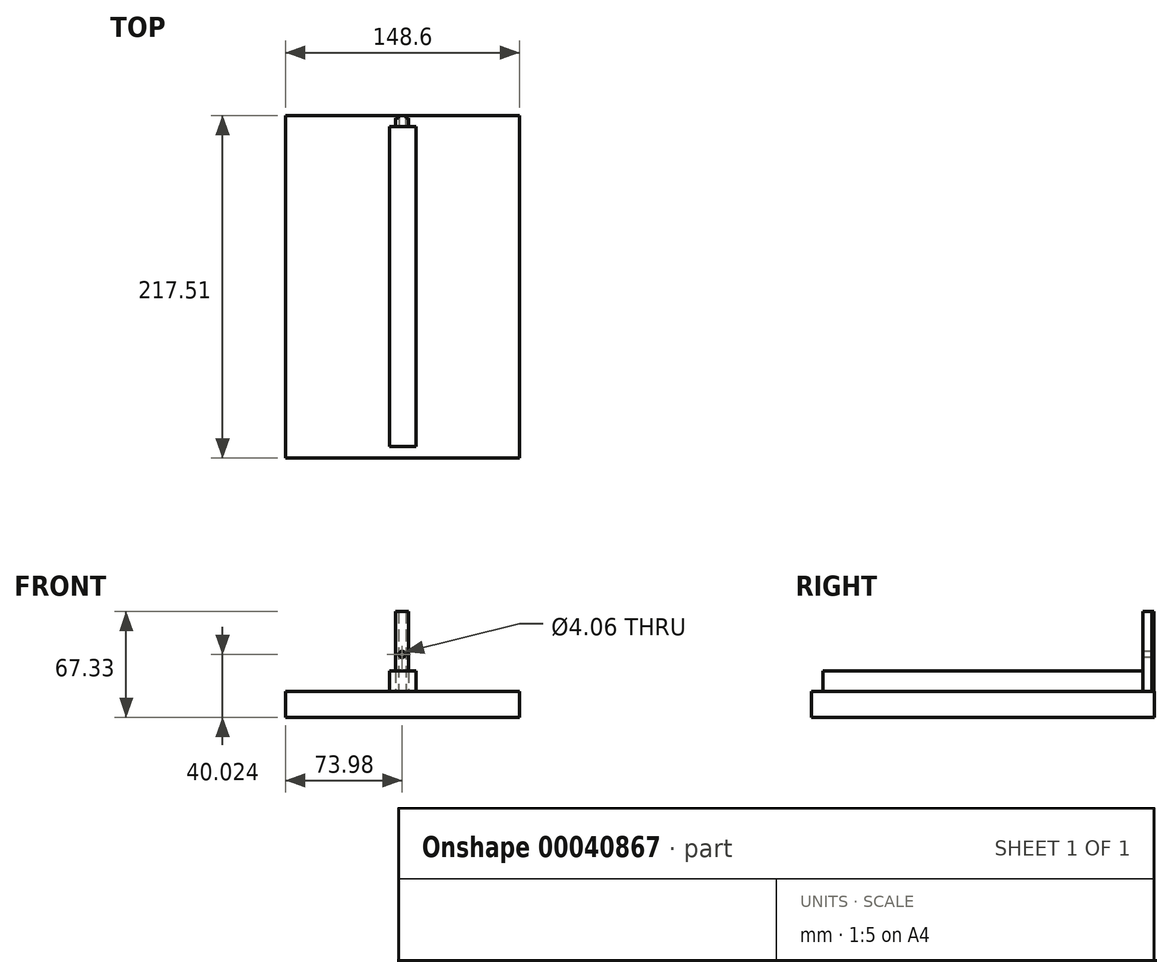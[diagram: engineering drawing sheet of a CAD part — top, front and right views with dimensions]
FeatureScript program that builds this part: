
annotation { "Feature Type Name" : "Feature", "Feature Type Description" : "" }
export const myFeature = defineFeature(function(context is Context, id is Id, definition is map)
    precondition{}
    {
        {
            var Q0;
            Q0=qCreatedBy(makeId("Top.planeOp"),FACE);
            var sketch = newSketch(context, id + "F0", { "sketchPlane" : qUnion([Q0])});
            skLineSegment(sketch, "E0.rect.bottom", {"start": v(4.76, -2.8) * mm, "end": v(-4.76, -2.8) * mm});
            skLineSegment(sketch, "E0.rect.top", {"start": v(4.76, 2.8) * mm, "end": v(2.98, 2.8) * mm});
            skPoint(sketch, "E0.rect.middle", {"position": v(0, 0) * mm});
            skPoint(sketch, "E1", {"position": v(2.98, 2.8) * mm});
            skPoint(sketch, "E2.MirrorP", {"position": v(-3.2, 2.8) * mm});
            skLineSegment(sketch, "E3.MirrorCS", {"start": v(0.01, 2.8) * mm, "end": v(0.01, 4.2) * mm});
            skLineSegment(sketch, "E4", {"start": v(0.01, 4.2) * mm, "end": v(2.98, 4.2) * mm});
            skPoint(sketch, "E5.orphan", {"position": v(0, 4.1) * mm});
            skLineSegment(sketch, "E6.trimOffspring", {"start": v(0.01, 2.8) * mm, "end": v(-4.76, 2.8) * mm});
            skLineSegment(sketch, "E7", {"start": v(0, 4.1) * mm, "end": v(0, 5.18) * mm});
            skLineSegment(sketch, "E8.MirrorCS", {"start": v(-0.01, 4.2) * mm, "end": v(-2.98, 4.2) * mm});
            skLineSegment(sketch, "E9.MirrorCS", {"start": v(-0.01, 2.8) * mm, "end": v(-0.01, 4.2) * mm});
            skLineSegment(sketch, "E10", {"start": v(-0.01, 4.2) * mm, "end": v(0.01, 4.2) * mm});
            skLineSegment(sketch, "E11", {"start": v(-2.36, 4.2) * mm, "end": v(-2.36, 2.8) * mm});
            skLineSegment(sketch, "E12", {"start": v(2.98, 2.8) * mm, "end": v(-0.01, 2.8) * mm});
            skLineSegment(sketch, "E13", {"start": v(2.36, 4.2) * mm, "end": v(2.36, 2.8) * mm});
            skLineSegment(sketch, "E14", {"start": v(-4.13, 2.8) * mm, "end": v(-4.13, -2.8) * mm});
            skLineSegment(sketch, "E15", {"start": v(4.13, 2.8) * mm, "end": v(4.13, -2.8) * mm});
            skSolve(sketch);
        }
        {
            var Q0;
            Q0 = qSketchRegion(id + "F0", true);
            extrude(context, id + "F1", {"entities" : qUnion([Q0]), "depth" : 50.8 * mm});
        }
        {
            var Q0;
            Q0=makeQuery(id+"F1.opExtrude","SWEPT_FACE",FACE,{"disambiguationData":[OSD([sQuery(id+"F0.wireOp",EDGE,"E0.rect.bottom")])]});
            var sketch = newSketch(context, id + "F2", { "sketchPlane" : qUnion([Q0])});
            skCircle(sketch, "E16", {"center": v(0, 23.5) * mm, "radius": 2.03 * mm});
            skSolve(sketch);
        }
        {
            var Q0;
            Q0=sQuery(id+"F2.wireOp",VERTEX,"E16.center");
            var Q1;
            Q1=makeQuery(id+"F1.opExtrude","SWEPT_BODY",BODY,{"disambiguationData":[OSD([sQuery(id+"F0.wireOp",EDGE,"E0.rect.bottom"),sQuery(id+"F0.wireOp",EDGE,"E0.rect.top"),sQuery(id+"F0.wireOp",EDGE,"E4"),sQuery(id+"F0.wireOp",EDGE,"E6.trimOffspring"),sQuery(id+"F0.wireOp",EDGE,"E8.MirrorCS"),sQuery(id+"F0.wireOp",EDGE,"E10"),sQuery(id+"F0.wireOp",EDGE,"E11"),sQuery(id+"F0.wireOp",EDGE,"E12"),sQuery(id+"F0.wireOp",EDGE,"E13"),sQuery(id+"F0.wireOp",EDGE,"E14"),sQuery(id+"F0.wireOp",EDGE,"E15")])]});
            hole(context, id + "F3", {"style" : HoleStyle.SIMPLE, "holeDiameter" : 4.06 * mm, "endStyle" : HoleEndStyle.THROUGH, "locations" : qUnion([Q0]), "scope" : qUnion([Q1])});
        }
        {
            var Q0;
            Q0=makeQuery(id+"F1.opExtrude","SWEPT_FACE",FACE,{"disambiguationData":[OSD([sQuery(id+"F0.wireOp",EDGE,"E0.rect.bottom")])]});
            var sketch = newSketch(context, id + "F4", { "sketchPlane" : qUnion([Q0])});
            skLineSegment(sketch, "E17.rect.bottom", {"start": v(8.76, -0.02) * mm, "end": v(-8.12, -0.02) * mm});
            skLineSegment(sketch, "E17.rect.top", {"start": v(8.76, 12.93) * mm, "end": v(-8.12, 12.93) * mm});
            skLineSegment(sketch, "E17.rect.left", {"start": v(8.76, -0.02) * mm, "end": v(8.76, 12.93) * mm});
            skLineSegment(sketch, "E17.rect.right", {"start": v(-8.12, -0.02) * mm, "end": v(-8.12, 12.93) * mm});
            skPoint(sketch, "E17.rect.middle", {"position": v(0.32, 6.45) * mm});
            skSolve(sketch);
        }
        {
            var Q0;
            Q0 = qSketchRegion(id + "F4", true);
            extrude(context, id + "F5", {"entities" : qUnion([Q0]), "operationType" : NewBodyOperationType.ADD, "depth" : 203.2 * mm});
        }
        {
            var Q0;
            Q0=makeQuery(id+"F5.opExtrude","SWEPT_FACE",FACE,{"disambiguationData":[OSD([sQuery(id+"F4.wireOp",EDGE,"E17.rect.bottom")])]});
            var sketch = newSketch(context, id + "F6", { "sketchPlane" : qUnion([Q0])});
            skLineSegment(sketch, "E18.rect.bottom", {"start": v(74.62, 213.15) * mm, "end": v(-73.98, 213.15) * mm});
            skLineSegment(sketch, "E18.rect.top", {"start": v(74.62, -4.36) * mm, "end": v(-73.98, -4.36) * mm});
            skLineSegment(sketch, "E18.rect.left", {"start": v(74.62, 213.15) * mm, "end": v(74.62, -4.36) * mm});
            skLineSegment(sketch, "E18.rect.right", {"start": v(-73.98, 213.15) * mm, "end": v(-73.98, -4.36) * mm});
            skPoint(sketch, "E18.rect.middle", {"position": v(0.32, 104.4) * mm});
            skPoint(sketch, "E18.rect.middle.positionSnap0", {"position": v(8.76, 104.4) * mm});
            skPoint(sketch, "E18.rect.middle.positionSnap1", {"position": v(0.32, 2.8) * mm});
            skPoint(sketch, "E18.rect.centerSnap0", {"position": v(8.76, 104.4) * mm});
            skPoint(sketch, "E18.rect.centerSnap1", {"position": v(0.32, 2.8) * mm});
            skSolve(sketch);
        }
        {
            var Q0;
            Q0 = qSketchRegion(id + "F6", true);
            extrude(context, id + "F7", {"entities" : qUnion([Q0]), "operationType" : NewBodyOperationType.ADD, "depth" : 16.5 * mm});
        }
    });
